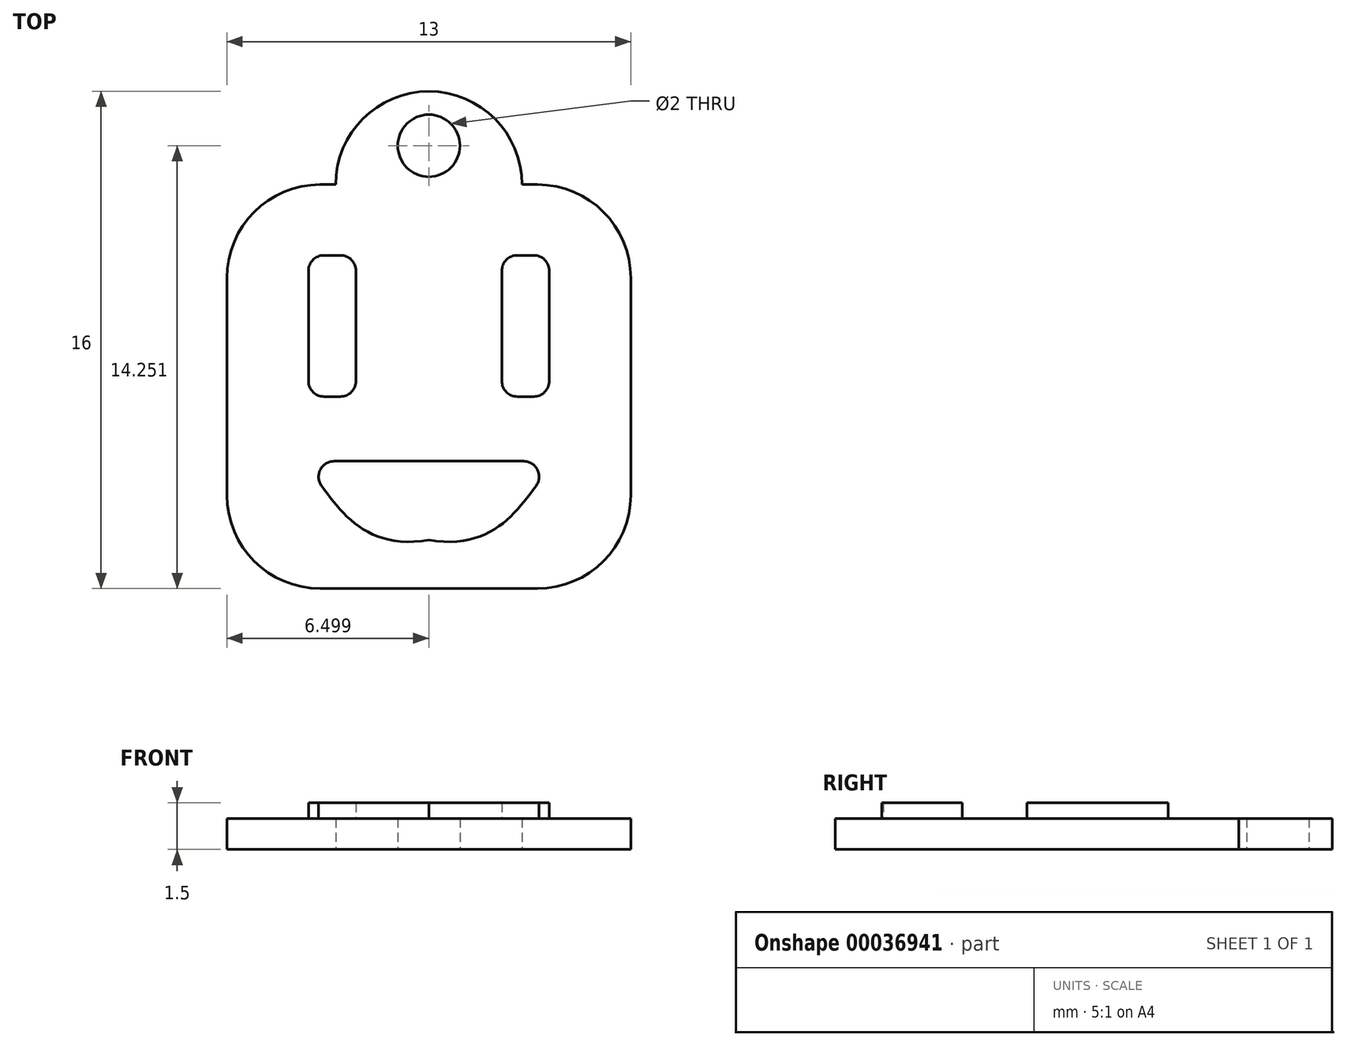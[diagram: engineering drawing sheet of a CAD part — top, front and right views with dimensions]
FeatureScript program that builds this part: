
annotation { "Feature Type Name" : "Feature", "Feature Type Description" : "" }
export const myFeature = defineFeature(function(context is Context, id is Id, definition is map)
    precondition{}
    {
        {
            var Q0;
            Q0=qCreatedBy(makeId("Top.planeOp"),FACE);
            var sketch = newSketch(context, id + "F0", { "sketchPlane" : qUnion([Q0])});
            skLineSegment(sketch, "E0.bottom", {"start": v(-38.63, -3.41) * mm, "end": v(-25.63, -3.41) * mm});
            skLineSegment(sketch, "E0.top", {"start": v(-38.63, -16.41) * mm, "end": v(-25.63, -16.41) * mm});
            skLineSegment(sketch, "E0.left", {"start": v(-38.63, -3.41) * mm, "end": v(-38.63, -16.41) * mm});
            skLineSegment(sketch, "E0.right", {"start": v(-25.63, -3.41) * mm, "end": v(-25.63, -16.41) * mm});
            skCircle(sketch, "E1", {"center": v(-32.13, -3.41) * mm, "radius": 3 * mm});
            skCircle(sketch, "E2", {"center": v(-32.13, -2.16) * mm, "radius": 1 * mm});
            skSolve(sketch);
        }
        {
            var Q0;
            Q0 = qSketchRegion(id + "F0", true);
            extrude(context, id + "F1", {"entities" : qUnion([Q0]), "depth" : 1 * mm});
        }
        {
            var Q0;
            Q0=makeQuery(id+"F1.opExtrude","SWEPT_EDGE",EDGE,{"disambiguationData":[OSD([sQuery(id+"F0.wireOp",EDGE,"E0.bottom"),sQuery(id+"F0.wireOp",EDGE,"E0.right")])]});
            var Q1;
            Q1=makeQuery(id+"F1.opExtrude","SWEPT_EDGE",EDGE,{"disambiguationData":[OSD([sQuery(id+"F0.wireOp",EDGE,"E0.top"),sQuery(id+"F0.wireOp",EDGE,"E0.right")])]});
            var Q2;
            Q2=makeQuery(id+"F1.opExtrude","SWEPT_EDGE",EDGE,{"disambiguationData":[OSD([sQuery(id+"F0.wireOp",EDGE,"E0.bottom"),sQuery(id+"F0.wireOp",EDGE,"E0.left")])]});
            var Q3;
            Q3=makeQuery(id+"F1.opExtrude","SWEPT_EDGE",EDGE,{"disambiguationData":[OSD([sQuery(id+"F0.wireOp",EDGE,"E0.top"),sQuery(id+"F0.wireOp",EDGE,"E0.left")])]});
            fillet(context, id + "F2", {"entities" : qUnion([Q0, Q1, Q2, Q3]), "radius" : 3 * mm, "tangentPropagation" : true, "allowEdgeOverflow" : false});
        }
        {
            var Q0;
            Q0=makeQuery(id+"F1.opExtrude","CAP_FACE",FACE,{"disambiguationData":[OSD([sQuery(id+"F0.wireOp",EDGE,"E0.bottom"),sQuery(id+"F0.wireOp",EDGE,"E0.top"),sQuery(id+"F0.wireOp",EDGE,"E0.left"),sQuery(id+"F0.wireOp",EDGE,"E0.right"),sQuery(id+"F0.wireOp",EDGE,"E1"),sQuery(id+"F0.wireOp",EDGE,"E2")])],"isStart":false});
            var sketch = newSketch(context, id + "F3", { "sketchPlane" : qUnion([Q0])});
            skLineSegment(sketch, "E3.bottom", {"start": v(-36, -5.69) * mm, "end": v(-34.48, -5.69) * mm});
            skLineSegment(sketch, "E3.top", {"start": v(-36, -10.23) * mm, "end": v(-34.48, -10.23) * mm});
            skLineSegment(sketch, "E3.left", {"start": v(-36, -5.69) * mm, "end": v(-36, -10.23) * mm});
            skLineSegment(sketch, "E3.right", {"start": v(-34.48, -5.69) * mm, "end": v(-34.48, -10.23) * mm});
            skLineSegment(sketch, "E4.MirrorCS", {"start": v(-29.78, -5.69) * mm, "end": v(-29.78, -10.23) * mm});
            skLineSegment(sketch, "E5.MirrorCS", {"start": v(-28.26, -5.69) * mm, "end": v(-28.26, -10.23) * mm});
            skLineSegment(sketch, "E6.MirrorCS", {"start": v(-28.26, -5.69) * mm, "end": v(-29.78, -5.69) * mm});
            skLineSegment(sketch, "E7.MirrorCS", {"start": v(-28.26, -10.23) * mm, "end": v(-29.78, -10.23) * mm});
            skPoint(sketch, "E8.start.orphan", {"position": v(-32.13, -16.41) * mm});
            skLineSegment(sketch, "E9", {"start": v(-36.23, -12.31) * mm, "end": v(-32.13, -12.31) * mm});
            skLineSegment(sketch, "E10", {"start": v(-32.13, -3.41) * mm, "end": v(-32.13, -16.41) * mm});
            skFitSpline(sketch, "E11", {"points": [v(-36.23, -12.31) * mm, v(-32.13, -14.85) * mm], "startDerivative": vector(2.8, -2.75) * mm, "endDerivative": vector(7.56, 1.24) * mm});
            skFitSpline(sketch, "E12.MirrorCS", {"points": [v(-28.04, -12.31) * mm, v(-32.13, -14.85) * mm], "startDerivative": vector(-2.8, -2.75) * mm, "endDerivative": vector(-7.56, 1.24) * mm});
            skLineSegment(sketch, "E13.MirrorCS", {"start": v(-28.04, -12.31) * mm, "end": v(-32.13, -12.31) * mm});
            skSolve(sketch);
        }
        {
            var Q0;
            Q0=makeQuery(id+"F3.imprint","IMPRINT",FACE,{"disambiguationData":[TD([[makeQuery(id+"F3.imprint","IMPRINT",EDGE,{"derivedFrom":sQuery(id+"F3.wireOp",EDGE,"E3.bottom")}),-1.0]])]});
            var Q1;
            Q1=makeQuery(id+"F3.imprint","IMPRINT",FACE,{"disambiguationData":[TD([[makeQuery(id+"F3.imprint","IMPRINT",EDGE,{"derivedFrom":sQuery(id+"F3.wireOp",EDGE,"E4.MirrorCS")}),1.0]])]});
            var Q2;
            {var subQ1=sQuery(id+"F3.wireOp",EDGE,"E13.MirrorCS");Q2=makeQuery(id+"F3.imprint","IMPRINT",FACE,{"disambiguationData":[TD([[makeQuery(id+"F3.imprint","IMPRINT",EDGE,{"derivedFrom":subQ1}),1.0]])]});}
            var Q3;
            {var subQ2=sQuery(id+"F3.wireOp",EDGE,"E9");Q3=makeQuery(id+"F3.imprint","IMPRINT",FACE,{"disambiguationData":[TD([[makeQuery(id+"F3.imprint","IMPRINT",EDGE,{"derivedFrom":subQ2}),-1.0]])]});}
            extrude(context, id + "F4", {"entities" : qUnion([Q0, Q1, Q2, Q3]), "operationType" : NewBodyOperationType.ADD, "depth" : 0.5 * mm});
        }
        {
            var Q0;
            Q0=makeQuery(id+"F4.opExtrude","SWEPT_EDGE",EDGE,{"disambiguationData":[OSD([sQuery(id+"F3.wireOp",EDGE,"E3.bottom"),sQuery(id+"F3.wireOp",EDGE,"E3.left")])]});
            var Q1;
            Q1=makeQuery(id+"F4.opExtrude","SWEPT_EDGE",EDGE,{"disambiguationData":[OSD([sQuery(id+"F3.wireOp",EDGE,"E3.bottom"),sQuery(id+"F3.wireOp",EDGE,"E3.right")])]});
            var Q2;
            Q2=makeQuery(id+"F4.opExtrude","SWEPT_EDGE",EDGE,{"disambiguationData":[OSD([sQuery(id+"F3.wireOp",EDGE,"E3.top"),sQuery(id+"F3.wireOp",EDGE,"E3.right")])]});
            var Q3;
            Q3=makeQuery(id+"F4.opExtrude","SWEPT_EDGE",EDGE,{"disambiguationData":[OSD([sQuery(id+"F3.wireOp",EDGE,"E3.top"),sQuery(id+"F3.wireOp",EDGE,"E3.left")])]});
            var Q4;
            Q4=makeQuery(id+"F4.opExtrude","SWEPT_EDGE",EDGE,{"disambiguationData":[OSD([sQuery(id+"F3.wireOp",EDGE,"E5.MirrorCS"),sQuery(id+"F3.wireOp",EDGE,"E6.MirrorCS")])]});
            var Q5;
            Q5=makeQuery(id+"F4.opExtrude","SWEPT_EDGE",EDGE,{"disambiguationData":[OSD([sQuery(id+"F3.wireOp",EDGE,"E5.MirrorCS"),sQuery(id+"F3.wireOp",EDGE,"E7.MirrorCS")])]});
            var Q6;
            Q6=makeQuery(id+"F4.opExtrude","SWEPT_EDGE",EDGE,{"disambiguationData":[OSD([sQuery(id+"F3.wireOp",EDGE,"E4.MirrorCS"),sQuery(id+"F3.wireOp",EDGE,"E6.MirrorCS")])]});
            var Q7;
            Q7=makeQuery(id+"F4.opExtrude","SWEPT_EDGE",EDGE,{"disambiguationData":[OSD([sQuery(id+"F3.wireOp",EDGE,"E4.MirrorCS"),sQuery(id+"F3.wireOp",EDGE,"E7.MirrorCS")])]});
            var Q8;
            Q8=makeQuery(id+"F4.opExtrude","SWEPT_EDGE",EDGE,{"disambiguationData":[OSD([sQuery(id+"F3.wireOp",EDGE,"E9"),sQuery(id+"F3.wireOp",EDGE,"E11")])]});
            var Q9;
            Q9=makeQuery(id+"F4.opExtrude","SWEPT_EDGE",EDGE,{"disambiguationData":[OSD([sQuery(id+"F3.wireOp",EDGE,"E13.MirrorCS"),sQuery(id+"F3.wireOp",EDGE,"E12.MirrorCS")])]});
            fillet(context, id + "F5", {"entities" : qUnion([Q0, Q1, Q2, Q3, Q4, Q5, Q6, Q7, Q8, Q9]), "radius" : 0.5 * mm, "tangentPropagation" : true, "allowEdgeOverflow" : false});
        }
    });
